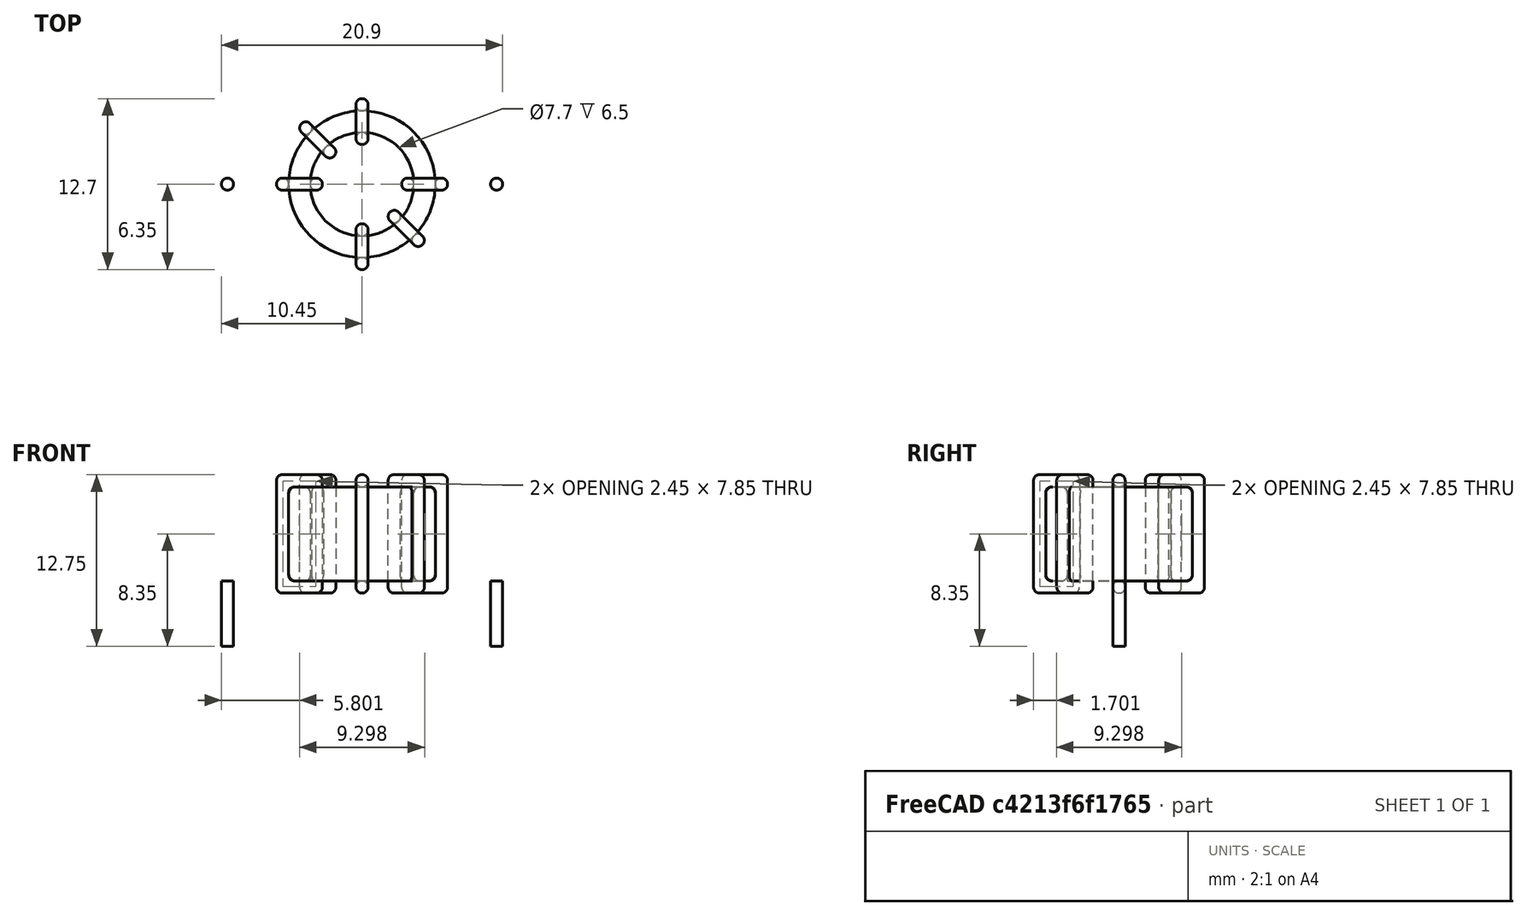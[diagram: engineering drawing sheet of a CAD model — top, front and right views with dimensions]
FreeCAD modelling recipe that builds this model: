
FCSTD DOCUMENT  (FreeCAD 0.16R6703 (Git))
Label: L_Toroid_Horizontal_D12.7mm_P20.00mm_Diameter14-5mm_Amidon-T50
License: All rights reserved
LicenseURL: http://en.wikipedia.org/wiki/All_rights_reserved
objects: Sketcher::SketchObject×6, PartDesign::Pad×6, PartDesign::Fillet×5, Spreadsheet::Sheet×1
note: 23 computed .brp shape members not serialized (recipe doc carries the construction recipe); baked Part::Feature solids carry a one-line shape summary decoded from their .brp

FEATURE [Spreadsheet::Sheet] Spreadsheet  label="dimensions"
  cells = A1=Wx; B1(Wx)=12.7; C1(WW)=7.696199999999999; D1=12.7; A2=Wy; B2(Wy)=12.7; D2=12.7; A3=RM; B3(RMx)=20; C3(RMy)=0; A4=d_wire; B4(d_wire)=0.8999999999999999; A5=H; B5(H)=7; A6=offsetx; B6(offsetx)=-3.65
FEATURE [Sketcher::SketchObject] Sketch
  Placement = pos=(0,0,1.4) rot=(0,0,1;0rad)
  expr: Placement.Base.z = 0.5 + Spreadsheet.d_wire
  expr: Constraints[0] = Spreadsheet.Wx / 2 - Spreadsheet.d_wire
  expr: Constraints[4] = Spreadsheet.WW / 2
  expr: Constraints[2] = Spreadsheet.RMy / 2
  expr: Constraints[1] = Spreadsheet.RMx / 2
  sketch-geometry (2):
    g0: Circle CenterX=10 CenterY=0 CenterZ=0 NormalX=0 NormalY=0 NormalZ=1 Radius=5.45
    g1: Circle CenterX=10 CenterY=0 CenterZ=0 NormalX=0 NormalY=0 NormalZ=1 Radius=3.8481
  constraints (5):
    c: Radius(g0) = 5.45
    c: DistanceX(g-1,g0) = 10
    c: DistanceY(g-1,g0) = 0
    c: Coincident(g1,g0)
    c: Radius(g1) = 3.8481
FEATURE [PartDesign::Pad] Pad
  Length = 7
  Length2 = 100
  Placement = pos=(0,0,1.4) rot=(0,0,1;0rad)
  Sketch = -> Sketch
  Type = 0
  expr: Length = Spreadsheet.H
FEATURE [Sketcher::SketchObject] Sketch001
  Placement = pos=(0,0,0.95) rot=(0,0,1;0rad)
  expr: Placement.Base.z = 0.5 + Spreadsheet.d_wire * 0.5
  expr: Constraints[4] = Spreadsheet.RMx
  expr: Constraints[2] = Spreadsheet.RMy
  expr: Constraints[1] = Spreadsheet.d_wire / 2
  sketch-geometry (2):
    g0: Circle CenterX=0 CenterY=0 CenterZ=0 NormalX=0 NormalY=0 NormalZ=1 Radius=0.45
    g1: Circle CenterX=20 CenterY=0 CenterZ=0 NormalX=0 NormalY=0 NormalZ=1 Radius=0.45
  constraints (5):
    c: Equal(g0,g1)
    c: Radius(g0) = 0.45
    c: DistanceY(g-1,g1) = 0
    c: Coincident(g0,g-1)
    c: DistanceX(g-1,g1) = 20
FEATURE [PartDesign::Pad] Pad001
  Length = 0.45
  Length2 = 4.4
  Placement = pos=(0,0,0.95) rot=(0,0,1;0rad)
  Reversed = true
  Sketch = -> Sketch001
  Type = 4
  expr: Length2 = 3.5 + Spreadsheet.d_wire
  expr: Length = Spreadsheet.d_wire / 2
FEATURE [PartDesign::Fillet] Fillet
  Base = -> Pad [Edge6,Edge3,Edge2]
  Placement = pos=(0,0,1.4) rot=(0,0,1;0rad)
  Radius = 0.5
FEATURE [Sketcher::SketchObject] Sketch003
  Placement = pos=(10,0,0) rot=(1,0,0;1.5708rad)
  expr: Placement.Base.x = Spreadsheet.RMx / 2
  expr: Constraints[49] = Spreadsheet.Wx - Spreadsheet.d_wire * 2
  expr: Constraints[44] = Spreadsheet.d_wire
  expr: Constraints[23] = Spreadsheet.H
  expr: Constraints[22] = Spreadsheet.Wx / 2 - Spreadsheet.d_wire
  expr: Placement.Base.y = Spreadsheet.RMy / 2
  expr: Constraints[21] = (Spreadsheet.Wx - Spreadsheet.WW) / 2 - Spreadsheet.d_wire
  expr: Constraints[19] = Spreadsheet.d_wire
  expr: Constraints[17] = Spreadsheet.d_wire
  expr: Constraints[18] = Spreadsheet.d_wire
  expr: Constraints[16] = Spreadsheet.d_wire
  sketch-geometry (16):
    g0: LineSegment StartX=-2.9481 StartY=0.5 StartZ=0 EndX=-6.35 EndY=0.5 EndZ=0
    g1: LineSegment StartX=-6.35 StartY=0.5 StartZ=0 EndX=-6.35 EndY=9.3 EndZ=0
    g2: LineSegment StartX=-6.35 StartY=9.3 StartZ=0 EndX=-2.9481 EndY=9.3 EndZ=0
    g3: LineSegment StartX=-2.9481 StartY=9.3 StartZ=0 EndX=-2.9481 EndY=0.5 EndZ=0
    g4: LineSegment StartX=-5.45 StartY=8.4 StartZ=0 EndX=-3.8481 EndY=8.4 EndZ=0
    g5: LineSegment StartX=-3.8481 StartY=8.4 StartZ=0 EndX=-3.8481 EndY=1.4 EndZ=0
    g6: LineSegment StartX=-3.8481 StartY=1.4 StartZ=0 EndX=-5.45 EndY=1.4 EndZ=0
    g7: LineSegment StartX=-5.45 StartY=1.4 StartZ=0 EndX=-5.45 EndY=8.4 EndZ=0
    g8: LineSegment StartX=2.9481 StartY=9.3 StartZ=0 EndX=6.35 EndY=9.3 EndZ=0
    g9: LineSegment StartX=6.35 StartY=9.3 StartZ=0 EndX=6.35 EndY=0.5 EndZ=0
    g10: LineSegment StartX=6.35 StartY=0.5 StartZ=0 EndX=2.9481 EndY=0.5 EndZ=0
    g11: LineSegment StartX=2.9481 StartY=0.5 StartZ=0 EndX=2.9481 EndY=9.3 EndZ=0
    g12: LineSegment StartX=3.8481 StartY=8.4 StartZ=0 EndX=5.45 EndY=8.4 EndZ=0
    g13: LineSegment StartX=5.45 StartY=8.4 StartZ=0 EndX=5.45 EndY=1.4 EndZ=0
    g14: LineSegment StartX=5.45 StartY=1.4 StartZ=0 EndX=3.8481 EndY=1.4 EndZ=0
    g15: LineSegment StartX=3.8481 StartY=1.4 StartZ=0 EndX=3.8481 EndY=8.4 EndZ=0
  constraints (50):
    c: Horizontal(g0)
    c: Coincident(g1,g0)
    c: Vertical(g1)
    c: Coincident(g2,g1)
    c: Horizontal(g2)
    c: Coincident(g3,g2)
    c: Coincident(g3,g0)
    c: Vertical(g3)
    c: Coincident(g4,g5)
    c: Coincident(g5,g6)
    c: Coincident(g6,g7)
    c: Coincident(g7,g4)
    c: Horizontal(g4)
    c: Horizontal(g6)
    c: Vertical(g5)
    c: Vertical(g7)
    c: DistanceX(g1,g4) = 0.9
    c: DistanceY(g4,g1) = 0.9
    c: DistanceX(g5,g0) = 0.9
    c: DistanceY(g0,g5) = 0.9
    c: DistanceY(g-1,g0) = 0.5
    c: DistanceX(g6,g6) = 1.6019
    c: DistanceX(g6,g-1) = 5.45
    c: DistanceY(g7,g7) = 7
    c: Coincident(g8,g9)
    c: Coincident(g9,g10)
    c: Coincident(g10,g11)
    c: Coincident(g11,g8)
    c: Horizontal(g8)
    c: Horizontal(g10)
    c: Vertical(g9)
    c: Vertical(g11)
    c: Coincident(g12,g13)
    c: Coincident(g13,g14)
    c: Coincident(g14,g15)
    c: Coincident(g15,g12)
    c: Horizontal(g12)
    c: Horizontal(g14)
    c: Vertical(g13)
    c: Vertical(g15)
    c: DistanceY(g8,g2) = 0
    c: DistanceY(g10,g0) = 0
    c: DistanceY(g14,g5) = 0
    c: DistanceY(g12,g4) = 0
    c: DistanceX(g8,g12) = 0.9
    c: Equal(g8,g2)
    c: Equal(g12,g4)
    c: Equal(g9,g1)
    c: Equal(g13,g7)
    c: DistanceX(g4,g12) = 10.9
FEATURE [PartDesign::Pad] Pad002
  Length = 0.9
  Length2 = 100
  Midplane = true
  Placement = pos=(10,0,0) rot=(1,0,0;1.5708rad)
  Sketch = -> Sketch003
  Type = 0
  expr: Length = Spreadsheet.d_wire
FEATURE [PartDesign::Fillet] Fillet001
  Base = -> Pad002 [Edge38,Edge41,Edge42,Edge43,Edge29,Edge32,Edge33,Edge34,Edge25,Edge35,Edge36,Edge13,Edge14,Edge15,Edge16,Edge17,Edge18,Edge19,Edge1,Edge2,Edge3,Edge4,Edge5,Edge6,Edge7,Edge37,Edge39,Edge40,Edge20,Edge23,Edge24,Edge21,Edge22,Edge8,Edge9,Edge10,Edge11,Edge12,Edge26,Edge27,+8 more]
  Placement = pos=(10,0,0) rot=(1,0,0;1.5708rad)
  Radius = 0.423
  expr: Radius = Spreadsheet.d_wire * 0.47
FEATURE [Sketcher::SketchObject] Sketch004
  Placement = pos=(10,0,0) rot=(0.862856,0.357407,0.357407;1.71777rad)
  expr: Placement.Base.x = Spreadsheet.RMx / 2
  expr: Constraints[49] = Spreadsheet.Wx - 2 * Spreadsheet.d_wire
  expr: Constraints[44] = Spreadsheet.d_wire
  expr: Constraints[23] = Spreadsheet.H
  expr: Constraints[22] = Spreadsheet.Wx / 2 - Spreadsheet.d_wire
  expr: Placement.Base.y = Spreadsheet.RMy / 2
  expr: Constraints[21] = (Spreadsheet.Wx - Spreadsheet.WW) / 2 - Spreadsheet.d_wire
  expr: Constraints[19] = Spreadsheet.d_wire
  expr: Constraints[17] = Spreadsheet.d_wire
  expr: Constraints[18] = Spreadsheet.d_wire
  expr: Constraints[16] = Spreadsheet.d_wire
  sketch-geometry (16):
    g0: LineSegment StartX=-2.9481 StartY=0.5 StartZ=0 EndX=-6.35 EndY=0.5 EndZ=0
    g1: LineSegment StartX=-6.35 StartY=0.5 StartZ=0 EndX=-6.35 EndY=9.3 EndZ=0
    g2: LineSegment StartX=-6.35 StartY=9.3 StartZ=0 EndX=-2.9481 EndY=9.3 EndZ=0
    g3: LineSegment StartX=-2.9481 StartY=9.3 StartZ=0 EndX=-2.9481 EndY=0.5 EndZ=0
    g4: LineSegment StartX=-5.45 StartY=8.4 StartZ=0 EndX=-3.8481 EndY=8.4 EndZ=0
    g5: LineSegment StartX=-3.8481 StartY=8.4 StartZ=0 EndX=-3.8481 EndY=1.4 EndZ=0
    g6: LineSegment StartX=-3.8481 StartY=1.4 StartZ=0 EndX=-5.45 EndY=1.4 EndZ=0
    g7: LineSegment StartX=-5.45 StartY=1.4 StartZ=0 EndX=-5.45 EndY=8.4 EndZ=0
    g8: LineSegment StartX=2.9481 StartY=9.3 StartZ=0 EndX=6.35 EndY=9.3 EndZ=0
    g9: LineSegment StartX=6.35 StartY=9.3 StartZ=0 EndX=6.35 EndY=0.5 EndZ=0
    g10: LineSegment StartX=6.35 StartY=0.5 StartZ=0 EndX=2.9481 EndY=0.5 EndZ=0
    g11: LineSegment StartX=2.9481 StartY=0.5 StartZ=0 EndX=2.9481 EndY=9.3 EndZ=0
    g12: LineSegment StartX=3.8481 StartY=8.4 StartZ=0 EndX=5.45 EndY=8.4 EndZ=0
    g13: LineSegment StartX=5.45 StartY=8.4 StartZ=0 EndX=5.45 EndY=1.4 EndZ=0
    g14: LineSegment StartX=5.45 StartY=1.4 StartZ=0 EndX=3.8481 EndY=1.4 EndZ=0
    g15: LineSegment StartX=3.8481 StartY=1.4 StartZ=0 EndX=3.8481 EndY=8.4 EndZ=0
  constraints (50):
    c: Horizontal(g0)
    c: Coincident(g1,g0)
    c: Vertical(g1)
    c: Coincident(g2,g1)
    c: Horizontal(g2)
    c: Coincident(g3,g2)
    c: Coincident(g3,g0)
    c: Vertical(g3)
    c: Coincident(g4,g5)
    c: Coincident(g5,g6)
    c: Coincident(g6,g7)
    c: Coincident(g7,g4)
    c: Horizontal(g4)
    c: Horizontal(g6)
    c: Vertical(g5)
    c: Vertical(g7)
    c: DistanceX(g1,g4) = 0.9
    c: DistanceY(g4,g1) = 0.9
    c: DistanceX(g5,g0) = 0.9
    c: DistanceY(g0,g5) = 0.9
    c: DistanceY(g-1,g0) = 0.5
    c: DistanceX(g6,g6) = 1.6019
    c: DistanceX(g6,g-1) = 5.45
    c: DistanceY(g7,g7) = 7
    c: Coincident(g8,g9)
    c: Coincident(g9,g10)
    c: Coincident(g10,g11)
    c: Coincident(g11,g8)
    c: Horizontal(g8)
    c: Horizontal(g10)
    c: Vertical(g9)
    c: Vertical(g11)
    c: Coincident(g12,g13)
    c: Coincident(g13,g14)
    c: Coincident(g14,g15)
    c: Coincident(g15,g12)
    c: Horizontal(g12)
    c: Horizontal(g14)
    c: Vertical(g13)
    c: Vertical(g15)
    c: DistanceY(g8,g2) = 0
    c: DistanceY(g10,g0) = 0
    c: DistanceY(g14,g5) = 0
    c: DistanceY(g12,g4) = 0
    c: DistanceX(g8,g12) = 0.9
    c: Equal(g8,g2)
    c: Equal(g12,g4)
    c: Equal(g9,g1)
    c: Equal(g13,g7)
    c: DistanceX(g4,g12) = 10.9
FEATURE [PartDesign::Pad] Pad003
  Length = 0.9
  Length2 = 100
  Midplane = true
  Placement = pos=(10,0,0) rot=(0.862856,0.357407,0.357407;1.71777rad)
  Sketch = -> Sketch004
  Type = 0
  expr: Length = Spreadsheet.d_wire
FEATURE [PartDesign::Fillet] Fillet002
  Base = -> Pad003 [Edge38,Edge41,Edge42,Edge43,Edge29,Edge32,Edge33,Edge34,Edge25,Edge35,Edge36,Edge13,Edge14,Edge15,Edge16,Edge17,Edge18,Edge19,Edge1,Edge2,Edge3,Edge4,Edge5,Edge6,Edge7,Edge37,Edge39,Edge40,Edge20,Edge23,Edge24,Edge21,Edge22,Edge8,Edge9,Edge10,Edge11,Edge12,Edge26,Edge27,+8 more]
  Placement = pos=(10,0,0) rot=(0.862856,0.357407,0.357407;1.71777rad)
  Radius = 0.423
  expr: Radius = Spreadsheet.d_wire * 0.47
FEATURE [Sketcher::SketchObject] Sketch005
  Placement = pos=(10,0,0) rot=(0.862856,-0.357407,-0.357407;1.71777rad)
  expr: Placement.Base.x = Spreadsheet.RMx / 2
  expr: Constraints[49] = Spreadsheet.Wx - 2 * Spreadsheet.d_wire
  expr: Constraints[44] = Spreadsheet.d_wire
  expr: Constraints[23] = Spreadsheet.H
  expr: Constraints[22] = Spreadsheet.Wx / 2 - Spreadsheet.d_wire
  expr: Placement.Base.y = Spreadsheet.RMy / 2
  expr: Constraints[21] = (Spreadsheet.Wx - Spreadsheet.WW) / 2 - Spreadsheet.d_wire
  expr: Constraints[19] = Spreadsheet.d_wire
  expr: Constraints[17] = Spreadsheet.d_wire
  expr: Constraints[18] = Spreadsheet.d_wire
  expr: Constraints[16] = Spreadsheet.d_wire
  sketch-geometry (16):
    g0: LineSegment StartX=-2.9481 StartY=0.5 StartZ=0 EndX=-6.35 EndY=0.5 EndZ=0
    g1: LineSegment StartX=-6.35 StartY=0.5 StartZ=0 EndX=-6.35 EndY=9.3 EndZ=0
    g2: LineSegment StartX=-6.35 StartY=9.3 StartZ=0 EndX=-2.9481 EndY=9.3 EndZ=0
    g3: LineSegment StartX=-2.9481 StartY=9.3 StartZ=0 EndX=-2.9481 EndY=0.5 EndZ=0
    g4: LineSegment StartX=-5.45 StartY=8.4 StartZ=0 EndX=-3.8481 EndY=8.4 EndZ=0
    g5: LineSegment StartX=-3.8481 StartY=8.4 StartZ=0 EndX=-3.8481 EndY=1.4 EndZ=0
    g6: LineSegment StartX=-3.8481 StartY=1.4 StartZ=0 EndX=-5.45 EndY=1.4 EndZ=0
    g7: LineSegment StartX=-5.45 StartY=1.4 StartZ=0 EndX=-5.45 EndY=8.4 EndZ=0
    g8: LineSegment StartX=2.9481 StartY=9.3 StartZ=0 EndX=6.35 EndY=9.3 EndZ=0
    g9: LineSegment StartX=6.35 StartY=9.3 StartZ=0 EndX=6.35 EndY=0.5 EndZ=0
    g10: LineSegment StartX=6.35 StartY=0.5 StartZ=0 EndX=2.9481 EndY=0.5 EndZ=0
    g11: LineSegment StartX=2.9481 StartY=0.5 StartZ=0 EndX=2.9481 EndY=9.3 EndZ=0
    g12: LineSegment StartX=3.8481 StartY=8.4 StartZ=0 EndX=5.45 EndY=8.4 EndZ=0
    g13: LineSegment StartX=5.45 StartY=8.4 StartZ=0 EndX=5.45 EndY=1.4 EndZ=0
    g14: LineSegment StartX=5.45 StartY=1.4 StartZ=0 EndX=3.8481 EndY=1.4 EndZ=0
    g15: LineSegment StartX=3.8481 StartY=1.4 StartZ=0 EndX=3.8481 EndY=8.4 EndZ=0
  constraints (50):
    c: Horizontal(g0)
    c: Coincident(g1,g0)
    c: Vertical(g1)
    c: Coincident(g2,g1)
    c: Horizontal(g2)
    c: Coincident(g3,g2)
    c: Coincident(g3,g0)
    c: Vertical(g3)
    c: Coincident(g4,g5)
    c: Coincident(g5,g6)
    c: Coincident(g6,g7)
    c: Coincident(g7,g4)
    c: Horizontal(g4)
    c: Horizontal(g6)
    c: Vertical(g5)
    c: Vertical(g7)
    c: DistanceX(g1,g4) = 0.9
    c: DistanceY(g4,g1) = 0.9
    c: DistanceX(g5,g0) = 0.9
    c: DistanceY(g0,g5) = 0.9
    c: DistanceY(g-1,g0) = 0.5
    c: DistanceX(g6,g6) = 1.6019
    c: DistanceX(g6,g-1) = 5.45
    c: DistanceY(g7,g7) = 7
    c: Coincident(g8,g9)
    c: Coincident(g9,g10)
    c: Coincident(g10,g11)
    c: Coincident(g11,g8)
    c: Horizontal(g8)
    c: Horizontal(g10)
    c: Vertical(g9)
    c: Vertical(g11)
    c: Coincident(g12,g13)
    c: Coincident(g13,g14)
    c: Coincident(g14,g15)
    c: Coincident(g15,g12)
    c: Horizontal(g12)
    c: Horizontal(g14)
    c: Vertical(g13)
    c: Vertical(g15)
    c: DistanceY(g8,g2) = 0
    c: DistanceY(g10,g0) = 0
    c: DistanceY(g14,g5) = 0
    c: DistanceY(g12,g4) = 0
    c: DistanceX(g8,g12) = 0.9
    c: Equal(g8,g2)
    c: Equal(g12,g4)
    c: Equal(g9,g1)
    c: Equal(g13,g7)
    c: DistanceX(g4,g12) = 10.9
FEATURE [PartDesign::Pad] Pad004
  Length = 0.9
  Length2 = 100
  Midplane = true
  Placement = pos=(10,0,0) rot=(0.862856,-0.357407,-0.357407;1.71777rad)
  Sketch = -> Sketch005
  Type = 0
  expr: Length = Spreadsheet.d_wire
FEATURE [PartDesign::Fillet] Fillet003
  Base = -> Pad004 [Edge38,Edge41,Edge42,Edge43,Edge29,Edge32,Edge33,Edge34,Edge25,Edge35,Edge36,Edge13,Edge14,Edge15,Edge16,Edge17,Edge18,Edge19,Edge1,Edge2,Edge3,Edge4,Edge5,Edge6,Edge7,Edge37,Edge39,Edge40,Edge20,Edge23,Edge24,Edge21,Edge22,Edge8,Edge9,Edge10,Edge11,Edge12,Edge26,Edge27,+8 more]
  Placement = pos=(10,0,0) rot=(0.862856,-0.357407,-0.357407;1.71777rad)
  Radius = 0.423
  expr: Radius = Spreadsheet.d_wire * 0.47
FEATURE [Sketcher::SketchObject] Sketch006
  Placement = pos=(10,0,0) rot=(0.57735,0.57735,0.57735;2.0944rad)
  expr: Placement.Base.x = Spreadsheet.RMx / 2
  expr: Constraints[49] = Spreadsheet.Wx - Spreadsheet.d_wire * 2
  expr: Constraints[44] = Spreadsheet.d_wire
  expr: Constraints[23] = Spreadsheet.H
  expr: Constraints[22] = Spreadsheet.Wx / 2 - Spreadsheet.d_wire
  expr: Placement.Base.y = Spreadsheet.RMy / 2
  expr: Constraints[21] = (Spreadsheet.Wx - Spreadsheet.WW) / 2 - Spreadsheet.d_wire
  expr: Constraints[19] = Spreadsheet.d_wire
  expr: Constraints[17] = Spreadsheet.d_wire
  expr: Constraints[18] = Spreadsheet.d_wire
  expr: Constraints[16] = Spreadsheet.d_wire
  sketch-geometry (16):
    g0: LineSegment StartX=-2.9481 StartY=0.5 StartZ=0 EndX=-6.35 EndY=0.5 EndZ=0
    g1: LineSegment StartX=-6.35 StartY=0.5 StartZ=0 EndX=-6.35 EndY=9.3 EndZ=0
    g2: LineSegment StartX=-6.35 StartY=9.3 StartZ=0 EndX=-2.9481 EndY=9.3 EndZ=0
    g3: LineSegment StartX=-2.9481 StartY=9.3 StartZ=0 EndX=-2.9481 EndY=0.5 EndZ=0
    g4: LineSegment StartX=-5.45 StartY=8.4 StartZ=0 EndX=-3.8481 EndY=8.4 EndZ=0
    g5: LineSegment StartX=-3.8481 StartY=8.4 StartZ=0 EndX=-3.8481 EndY=1.4 EndZ=0
    g6: LineSegment StartX=-3.8481 StartY=1.4 StartZ=0 EndX=-5.45 EndY=1.4 EndZ=0
    g7: LineSegment StartX=-5.45 StartY=1.4 StartZ=0 EndX=-5.45 EndY=8.4 EndZ=0
    g8: LineSegment StartX=2.9481 StartY=9.3 StartZ=0 EndX=6.35 EndY=9.3 EndZ=0
    g9: LineSegment StartX=6.35 StartY=9.3 StartZ=0 EndX=6.35 EndY=0.5 EndZ=0
    g10: LineSegment StartX=6.35 StartY=0.5 StartZ=0 EndX=2.9481 EndY=0.5 EndZ=0
    g11: LineSegment StartX=2.9481 StartY=0.5 StartZ=0 EndX=2.9481 EndY=9.3 EndZ=0
    g12: LineSegment StartX=3.8481 StartY=8.4 StartZ=0 EndX=5.45 EndY=8.4 EndZ=0
    g13: LineSegment StartX=5.45 StartY=8.4 StartZ=0 EndX=5.45 EndY=1.4 EndZ=0
    g14: LineSegment StartX=5.45 StartY=1.4 StartZ=0 EndX=3.8481 EndY=1.4 EndZ=0
    g15: LineSegment StartX=3.8481 StartY=1.4 StartZ=0 EndX=3.8481 EndY=8.4 EndZ=0
  constraints (50):
    c: Horizontal(g0)
    c: Coincident(g1,g0)
    c: Vertical(g1)
    c: Coincident(g2,g1)
    c: Horizontal(g2)
    c: Coincident(g3,g2)
    c: Coincident(g3,g0)
    c: Vertical(g3)
    c: Coincident(g4,g5)
    c: Coincident(g5,g6)
    c: Coincident(g6,g7)
    c: Coincident(g7,g4)
    c: Horizontal(g4)
    c: Horizontal(g6)
    c: Vertical(g5)
    c: Vertical(g7)
    c: DistanceX(g1,g4) = 0.9
    c: DistanceY(g4,g1) = 0.9
    c: DistanceX(g5,g0) = 0.9
    c: DistanceY(g0,g5) = 0.9
    c: DistanceY(g-1,g0) = 0.5
    c: DistanceX(g6,g6) = 1.6019
    c: DistanceX(g6,g-1) = 5.45
    c: DistanceY(g7,g7) = 7
    c: Coincident(g8,g9)
    c: Coincident(g9,g10)
    c: Coincident(g10,g11)
    c: Coincident(g11,g8)
    c: Horizontal(g8)
    c: Horizontal(g10)
    c: Vertical(g9)
    c: Vertical(g11)
    c: Coincident(g12,g13)
    c: Coincident(g13,g14)
    c: Coincident(g14,g15)
    c: Coincident(g15,g12)
    c: Horizontal(g12)
    c: Horizontal(g14)
    c: Vertical(g13)
    c: Vertical(g15)
    c: DistanceY(g8,g2) = 0
    c: DistanceY(g10,g0) = 0
    c: DistanceY(g14,g5) = 0
    c: DistanceY(g12,g4) = 0
    c: DistanceX(g8,g12) = 0.9
    c: Equal(g8,g2)
    c: Equal(g12,g4)
    c: Equal(g9,g1)
    c: Equal(g13,g7)
    c: DistanceX(g4,g12) = 10.9
FEATURE [PartDesign::Pad] Pad005
  Length = 0.9
  Length2 = 100
  Midplane = true
  Placement = pos=(10,0,0) rot=(0.57735,0.57735,0.57735;2.0944rad)
  Sketch = -> Sketch006
  Type = 0
  expr: Length = Spreadsheet.d_wire
FEATURE [PartDesign::Fillet] Fillet004
  Base = -> Pad005 [Edge38,Edge41,Edge42,Edge43,Edge29,Edge32,Edge33,Edge34,Edge25,Edge35,Edge36,Edge13,Edge14,Edge15,Edge16,Edge17,Edge18,Edge19,Edge1,Edge2,Edge3,Edge4,Edge5,Edge6,Edge7,Edge37,Edge39,Edge40,Edge20,Edge23,Edge24,Edge21,Edge22,Edge8,Edge9,Edge10,Edge11,Edge12,Edge26,Edge27,+8 more]
  Placement = pos=(10,0,0) rot=(0.57735,0.57735,0.57735;2.0944rad)
  Radius = 0.423
  expr: Radius = Spreadsheet.d_wire * 0.47
